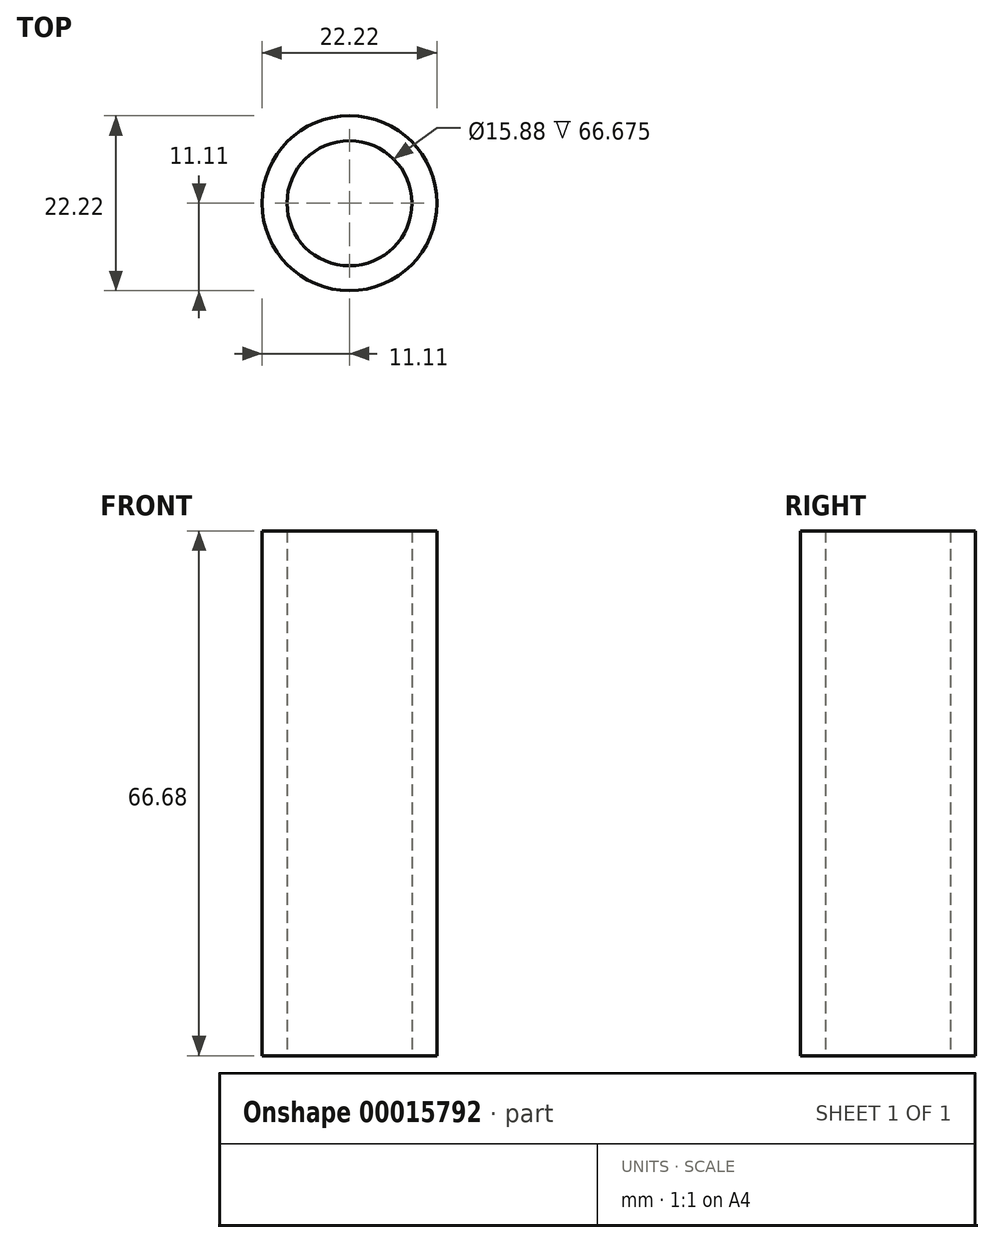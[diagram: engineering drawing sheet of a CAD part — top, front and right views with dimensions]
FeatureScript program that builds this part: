
annotation { "Feature Type Name" : "Feature", "Feature Type Description" : "" }
export const myFeature = defineFeature(function(context is Context, id is Id, definition is map)
    precondition{}
    {
        {
            var Q0;
            Q0=qCreatedBy(makeId("Top.planeOp"),FACE);
            var sketch = newSketch(context, id + "F0", { "sketchPlane" : qUnion([Q0])});
            skCircle(sketch, "E0", {"center": v(0, 0) * mm, "radius": 11.11 * mm});
            skCircle(sketch, "E1", {"center": v(0, 0) * mm, "radius": 7.94 * mm});
            skSolve(sketch);
        }
        {
            var Q0;
            Q0=qSketchRegion(id+"F0",true);
            extrude(context, id + "F1", {"entities" : qUnion([Q0]), "depth" : 66.67 * mm});
        }
    });
